# Revit family: Hager-FW-IP30-With_Door-With_notch-syst-CH-de
name_source: partatom
category: Electrical Equipment
units: mm (PartAtom-declared; Revit-internal decimal feet)

## family parameters
Cut with Voids When Loaded = No
Host = Face
Panel Configuration = Two Columns, Circuits Across
Part Type = Panelboard
Room Calculation Point = No
Round Connector Dimension = Use Diameter
Shared = No

## types (20) — shared parameters
EF000003 - Montageart = EV000128 - Hohlwand
EF000007 - Farbe = EV000202 - weiß
EF000049 - Tiefe = 125 mm  [stored 0.410105 ft]
EF000116 - RAL-Nummer = 9010
EF000218 - Einbautiefe = 112 mm  [stored 0.367454 ft]
EF000339 - Art der Abdeckung = EV004216 - Tür
EF001062 - EMV-Ausführung = No
EF001088 - Anbaumöglichkeit = Yes
EF001131 - Innentiefe = 112 mm  [stored 0.367454 ft]
EF001134 - DIN-Schiene = Yes
EF001596 - Werkstoff des Gehäuses = EV000179 - Stahl
EF002950 - Breite in Teilungseinheiten = 12
EF004462 - Art der Schließung = EV000154 - sonstige
EF005474 - Schutzart (IP) = EV006410 - IP30
EF006244 - Transparenter Deckel/Tür = No
EF006306 - Mit Schloss = No
EF009212 - Ausführung Deckel = EV009916 - mit Ausschnitt
EF015776 - Erdungsklemmenblock = No
EF015777 - Neutralleiterklemmenblock = No
EF015941 - Signaldurchlassende Tür = No
HG000002 - Mit tür = Yes
HG000003 - Bereich = FW
HG000005 - Dicke = 3 mm  [stored 0.00984252 ft]
HG000006 - Unterputz = Yes
HG000011 - Leere Reihen von unten = No
HG000017 - Distanz zwischen den Polen = 18 mm  [stored 0.0590551 ft]
Manufacturer = Hager
Type Comments = FW
zero-valued in all types: Default Elevation

## per-type parameters (varying)
| type | EF000008 - Breite | EF000040 - Höhe | EF000118 - Mit Montageplatte | EF000266 - Anzahl der Reihen | EF000332 - Einbauhöhe | EF000846 - Einbaubreite | HG000001 - Anzahl der Spalten | HG000004 - Herstellerreferenz | HG000007 - Anzahl der leeren Spalten | HG000008 - Anzahl der leeren Reihen | HG000009 - Doppelflügeligen Tür | HG000010 - Asymmetrische Türen | Model |
| Unterputz IP30 B353 H1003 T125 12 Teilungseinheiten - FWU61S1 | 353 mm  [stored 1.15814 ft] | 1003 mm  [stored 3.29068 ft] | No | 6 | 952 mm  [stored 3.12336 ft] | 310 mm  [stored 1.01706 ft] | 1 | FWU61S1 | 0 | 0 | No | No | FWU61S1 |
| Unterputz IP30 B353 H1153 T125 12 Teilungseinheiten - FWU71S1 | 353 mm  [stored 1.15814 ft] | 1153 mm | No | 7 | 1102 mm  [stored 3.61549 ft] | 310 mm  [stored 1.01706 ft] | 1 | FWU71S1 | 0 | 0 | No | No | FWU71S1 |
| Unterputz IP30 B353 H553 T125 12 Teilungseinheiten - FWU31S1 | 353 mm  [stored 1.15814 ft] | 553 mm  [stored 1.8143 ft] | No | 3 | 502 mm  [stored 1.64698 ft] | 310 mm  [stored 1.01706 ft] | 1 | FWU31S1 | 0 | 0 | No | No | FWU31S1 |
| Unterputz IP30 B353 H703 T125 12 Teilungseinheiten - FWU41S1 | 353 mm  [stored 1.15814 ft] | 703 mm  [stored 2.30643 ft] | No | 4 | 652 mm  [stored 2.13911 ft] | 310 mm  [stored 1.01706 ft] | 1 | FWU41S1 | 0 | 0 | No | No | FWU41S1 |
| Unterputz IP30 B353 H853 T125 12 Teilungseinheiten - FWU51S1 | 353 mm  [stored 1.15814 ft] | 853 mm  [stored 2.79856 ft] | No | 5 | 802 mm  [stored 2.63123 ft] | 310 mm  [stored 1.01706 ft] | 1 | FWU51S1 | 0 | 0 | No | No | FWU51S1 |
| Unterputz IP30 B603 H1003 T125 12 Teilungseinheiten - FWU62K | 603 mm | 1003 mm  [stored 3.29068 ft] | Yes | 6 | 952 mm  [stored 3.12336 ft] | 560 mm  [stored 1.83727 ft] | 1 | FWU62K | 1 | 6 | No | No | FWU62K |
| Unterputz IP30 B603 H1003 T125 12 Teilungseinheiten - FWU62S1 | 603 mm | 1003 mm  [stored 3.29068 ft] | No | 12 | 952 mm  [stored 3.12336 ft] | 560 mm  [stored 1.83727 ft] | 2 | FWU62S1 | 0 | 0 | No | No | FWU62S1 |
| Unterputz IP30 B603 H1153 T125 12 Teilungseinheiten - FWU72S1 | 603 mm | 1153 mm | No | 14 | 1102 mm  [stored 3.61549 ft] | 560 mm  [stored 1.83727 ft] | 2 | FWU72S1 | 0 | 0 | No | No | FWU72S1 |
| Unterputz IP30 B603 H553 T125 12 Teilungseinheiten - FWU32S1 | 603 mm | 553 mm  [stored 1.8143 ft] | No | 6 | 502 mm  [stored 1.64698 ft] | 560 mm  [stored 1.83727 ft] | 2 | FWU32S1 | 0 | 0 | No | No | FWU32S1 |
| Unterputz IP30 B603 H703 T125 12 Teilungseinheiten - FWU42K | 603 mm | 703 mm  [stored 2.30643 ft] | Yes | 4 | 652 mm  [stored 2.13911 ft] | 560 mm  [stored 1.83727 ft] | 1 | FWU42K | 1 | 4 | No | No | FWU42K |
| Unterputz IP30 B603 H703 T125 12 Teilungseinheiten - FWU42S1 | 603 mm | 703 mm  [stored 2.30643 ft] | No | 8 | 652 mm  [stored 2.13911 ft] | 560 mm  [stored 1.83727 ft] | 2 | FWU42S1 | 0 | 0 | No | No | FWU42S1 |
| Unterputz IP30 B603 H853 T125 12 Teilungseinheiten - FWU52K | 603 mm | 853 mm  [stored 2.79856 ft] | Yes | 5 | 802 mm  [stored 2.63123 ft] | 560 mm  [stored 1.83727 ft] | 1 | FWU52K | 1 | 5 | No | No | FWU52K |
| Unterputz IP30 B603 H853 T125 12 Teilungseinheiten - FWU52S1 | 603 mm | 853 mm  [stored 2.79856 ft] | No | 10 | 802 mm  [stored 2.63123 ft] | 560 mm  [stored 1.83727 ft] | 2 | FWU52S1 | 0 | 0 | No | No | FWU52S1 |
| Unterputz IP30 B853 H1003 T125 12 Teilungseinheiten - FWU63S1 | 853 mm  [stored 2.79856 ft] | 1003 mm  [stored 3.29068 ft] | No | 18 | 952 mm  [stored 3.12336 ft] | 810 mm | 3 | FWU63S1 | 0 | 0 | Yes | Yes | FWU63S1 |
| Unterputz IP30 B853 H1153 T125 12 Teilungseinheiten - FWU73S1 | 853 mm  [stored 2.79856 ft] | 1153 mm | No | 21 | 1102 mm  [stored 3.61549 ft] | 810 mm | 3 | FWU73S1 | 0 | 0 | Yes | Yes | FWU73S1 |
| Unterputz IP30 B853 H553 T125 12 Teilungseinheiten - FWU33S1 | 853 mm  [stored 2.79856 ft] | 553 mm  [stored 1.8143 ft] | No | 9 | 502 mm  [stored 1.64698 ft] | 810 mm | 3 | FWU33S1 | 0 | 0 | Yes | Yes | FWU33S1 |
| Unterputz IP30 B853 H703 T125 12 Teilungseinheiten - FWU43K | 853 mm  [stored 2.79856 ft] | 703 mm  [stored 2.30643 ft] | Yes | 8 | 652 mm  [stored 2.13911 ft] | 810 mm | 2 | FWU43K | 1 | 4 | Yes | Yes | FWU43K |
| Unterputz IP30 B853 H703 T125 12 Teilungseinheiten - FWU43S1 | 853 mm  [stored 2.79856 ft] | 703 mm  [stored 2.30643 ft] | No | 12 | 652 mm  [stored 2.13911 ft] | 810 mm | 3 | FWU43S1 | 0 | 0 | Yes | Yes | FWU43S1 |
| Unterputz IP30 B853 H853 T125 12 Teilungseinheiten - FWU53K | 853 mm  [stored 2.79856 ft] | 853 mm  [stored 2.79856 ft] | Yes | 10 | 802 mm  [stored 2.63123 ft] | 810 mm | 2 | FWU53K | 1 | 5 | Yes | Yes | FWU53K |
| Unterputz IP30 B853 H853 T125 12 Teilungseinheiten - FWU53S1 | 853 mm  [stored 2.79856 ft] | 853 mm  [stored 2.79856 ft] | No | 15 | 802 mm  [stored 2.63123 ft] | 810 mm | 3 | FWU53S1 | 0 | 0 | Yes | Yes | FWU53S1 |

note: [stored X ft] marks values corroborated as IEEE doubles in the binary element streams (Revit-internal decimal feet)

## geometry (parser evidence)
native form markers: Sweep x17
no freeform markers — native parametric forms only
